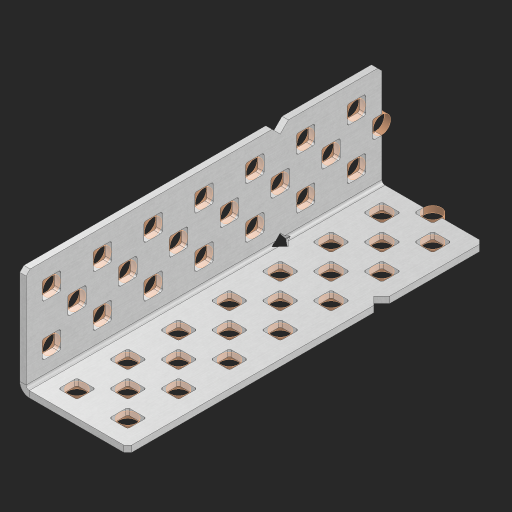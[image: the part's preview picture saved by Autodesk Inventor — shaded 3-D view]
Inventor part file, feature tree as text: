
AUTODESK INVENTOR PART (.ipt)
format: ipt  version: 2023 (Build 270158000, 158)  size: 859,136 bytes
history: native  units: in
note: dims shown in document units (in); Inventor stores cm internally (conversion verified against a paired STEP export)
features: other x48, extrude x40, sheet_metal_op x8, sketch x7, pattern_linear x2, mirror x1, chamfer x1
ambient origin geometry x8: Origin, YZ Plane, XZ Plane, XY Plane, X Axis, Y Axis, Z Axis, Center Point
bodies: Solid1 (feature_tree), Body (feature_tree)
feature tree (107):
  sheet_metal_op  "Flanges"
  sheet_metal_op  "Body Pattern"
  pattern_linear  "Center Pattern"  Spacing1=1.0in  [1 undecoded]
  other  "Arc Length"
  pattern_linear  "Notch Pattern"  Spacing1=0.25in  [1 undecoded]
  other  "Diagonal Plane"
  mirror  "Everything Mirrored"
  chamfer  "End Chamfer"
  sketch  "Sketch1"  dims[d0=1.0in]
  other  "Plate1"
  sketch  "Sketch2"  dims[d1=3.5in]
  other  "Plate2"
  sheet_metal_op  "Bend1"
  sheet_metal_op  "Corner1"
  sketch  "Sketch8"  dims[d2=0.0625in]
  sketch  "Sketch9"  dims[d3=0.0625in]
  other  "Srf91"
  sheet_metal_op  "Body Pattern Sketch"
  other  "Srf92"
  sketch  "Sketch13"  dims[d4=0.0312in]
  sketch  "Sketch15"  dims[d5=0.125in]
  sketch  "Sketch16"  dims[d6=0.0625in d7=1.0in d8=90.0deg d9=0.0312in d10=0.25in d11=0.0625in d12=0.0625in d49=0.182in d50=0.02in d52=0.25in d53=0.0625in d54=0.0in d55=0.172in d56=1.0in d57=0.0in d60=2.7559in d62=0.5in d63=0.7874in d65=0.5in d85=0.1473in d86=0.1782in d89=0.0625in d90=0.0in d91=0.04in d92=0.0491in d95=2.5in d96=0.04in d97=0.25in d98=45.0deg d99=0.25in d106=0.182in d107=0.02in d108=0.5in d110=0.0625in d111=0.0in d112=0.172in d113=0.5in d114=0.0in d117=0.5in d123=0.25in d125=0.25in d126=0.0491in d127=0.1473in d128=0.08in d129=0.04in d130=2.5in]
  other  "Srf786"
  other  "Srf856"
  other  "Srf857"
  other  "Srf858"
  other  "Srf859"
  other  "Srf860"
  other  "Srf861"
  other  "Srf889"
  other  "Srf890"
  other  "Srf891"
  other  "Srf1275"
  other  "Srf1276"
  other  "Srf1278"
  other  "Srf1279"
  other  "Srf1280"
  other  "Srf1281"
  other  "Srf1282"
  other  "Srf1283"
  other  "Srf1277"
  other  "Srf1285"
  other  "Srf1286"
  other  "Srf1287"
  other  "Srf1383"
  other  "Srf1384"
  other  "Srf1385"
  other  "Srf1386"
  other  "Srf1387"
  other  "Srf1388"
  other  "Srf1445"
  other  "Srf1446"
  other  "Srf1447"
  other  "Srf1475"
  other  "Srf1476"
  other  "Srf1477"
  other  "Srf1478"
  other  "Srf1479"
  other  "Srf1480"
  other  "Srf1537"
  other  "Srf1538"
  other  "Srf1539"
  sheet_metal_op  "Body Stamp"
  sheet_metal_op  "Body Circle"
  other  "Center Stamp"
  other  "Center Circle"
  sheet_metal_op  "Notch"
  extrude  "ExtrusionSrf92"  Depth=0.0625in
  extrude  "ExtrusionSrf856"  Depth=0.0625in
  extrude  "ExtrusionSrf857"  Depth=0.182in
  extrude  "ExtrusionSrf858"  Depth=0.02in
  extrude  "ExtrusionSrf859"  Depth=0.25in
  extrude  "ExtrusionSrf860"  Depth=0.0625in
  extrude  "ExtrusionSrf861"  TaperAngle=0.0deg  [1 undecoded]
  extrude  "ExtrusionSrf889"  Depth=2.5in
  extrude  "ExtrusionSrf890"  Depth=1.0in TaperAngle=0.0deg
  extrude  "ExtrusionSrf891"  Depth=2.5in
  extrude  "ExtrusionSrf1275"  Depth=0.5in
  extrude  "ExtrusionSrf1276"  Depth=2.5in
  extrude  "ExtrusionSrf1277"  Depth=2.5in
  extrude  "ExtrusionSrf1278"  Depth=0.0625in
  extrude  "ExtrusionSrf1279"  Depth=2.5in TaperAngle=0.0deg
  extrude  "ExtrusionSrf1280"  Depth=2.5in
  extrude  "ExtrusionSrf1281"  Depth=0.25in TaperAngle=45.0deg
  extrude  "ExtrusionSrf1282"  Depth=0.25in
  extrude  "ExtrusionSrf1345"  Depth=0.182in
  extrude  "ExtrusionSrf1346"  Depth=0.02in
  extrude  "ExtrusionSrf1347"  Depth=0.5in
  extrude  "ExtrusionSrf1348"  Depth=0.0625in
  extrude  "ExtrusionSrf1383"  TaperAngle=0.0deg  [1 undecoded]
  extrude  "ExtrusionSrf1384"  Depth=2.5in
  extrude  "ExtrusionSrf1385"  Depth=0.5in TaperAngle=0.0deg
  extrude  "ExtrusionSrf1386"  Depth=0.5in
  extrude  "ExtrusionSrf1387"  Depth=0.25in
  extrude  "ExtrusionSrf1388"  Depth=0.25in
  extrude  "ExtrusionSrf1445"  Depth=2.5in
  extrude  "ExtrusionSrf1446"  Depth=2.5in
  extrude  "ExtrusionSrf1447"  Depth=2.5in
  extrude  "ExtrusionSrf1475"  Depth=2.5in
  extrude  "ExtrusionSrf1476"  Depth=2.5in
  extrude  "ExtrusionSrf1477"  [1 undecoded]
  extrude  "ExtrusionSrf1478"  [1 undecoded]
  extrude  "ExtrusionSrf1479"  [1 undecoded]
  extrude  "ExtrusionSrf1480"  [1 undecoded]
  extrude  "ExtrusionSrf1537"  [1 undecoded]
  extrude  "ExtrusionSrf1538"  [1 undecoded]
  extrude  "ExtrusionSrf1539"  [1 undecoded]
note: 11 required parameter values undecoded (feature->parameter linkage not recoverable at this tier; creation-order binding heuristic only, values carry confidence <= 0.55)
